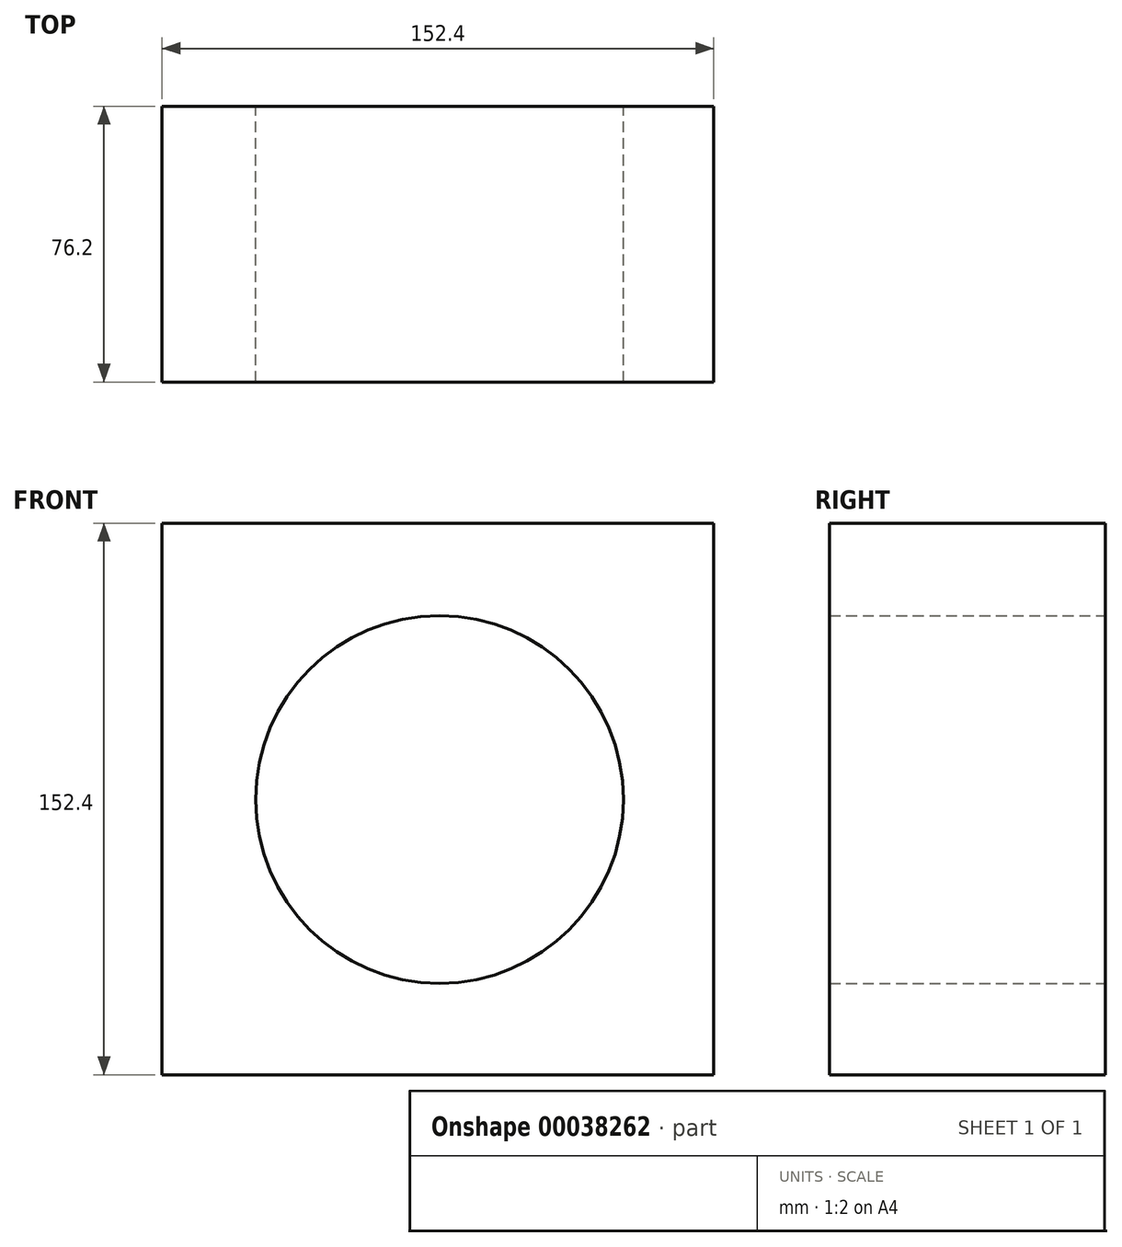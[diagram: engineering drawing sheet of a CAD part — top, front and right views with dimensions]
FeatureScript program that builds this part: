
annotation { "Feature Type Name" : "Feature", "Feature Type Description" : "" }
export const myFeature = defineFeature(function(context is Context, id is Id, definition is map)
    precondition{}
    {
        {
            var Q0;
            Q0=qCreatedBy(makeId("Front.planeOp"),FACE);
            var sketch = newSketch(context, id + "F0", { "sketchPlane" : qUnion([Q0])});
            skLineSegment(sketch, "E0.bottom", {"start": v(-76.63, -76.06) * mm, "end": v(75.77, -76.06) * mm});
            skLineSegment(sketch, "E0.top", {"start": v(-76.63, 76.34) * mm, "end": v(75.77, 76.34) * mm});
            skLineSegment(sketch, "E0.left", {"start": v(-76.63, -76.06) * mm, "end": v(-76.63, 76.34) * mm});
            skLineSegment(sketch, "E0.right", {"start": v(75.77, -76.06) * mm, "end": v(75.77, 76.34) * mm});
            skCircle(sketch, "E1", {"center": v(0, 0) * mm, "radius": 50.8 * mm});
            skSolve(sketch);
        }
        {
            var Q0;
            Q0 = qSketchRegion(id + "F0", true);
            extrude(context, id + "F1", {"entities" : qUnion([Q0]), "depth" : 76.2 * mm});
        }
    });
